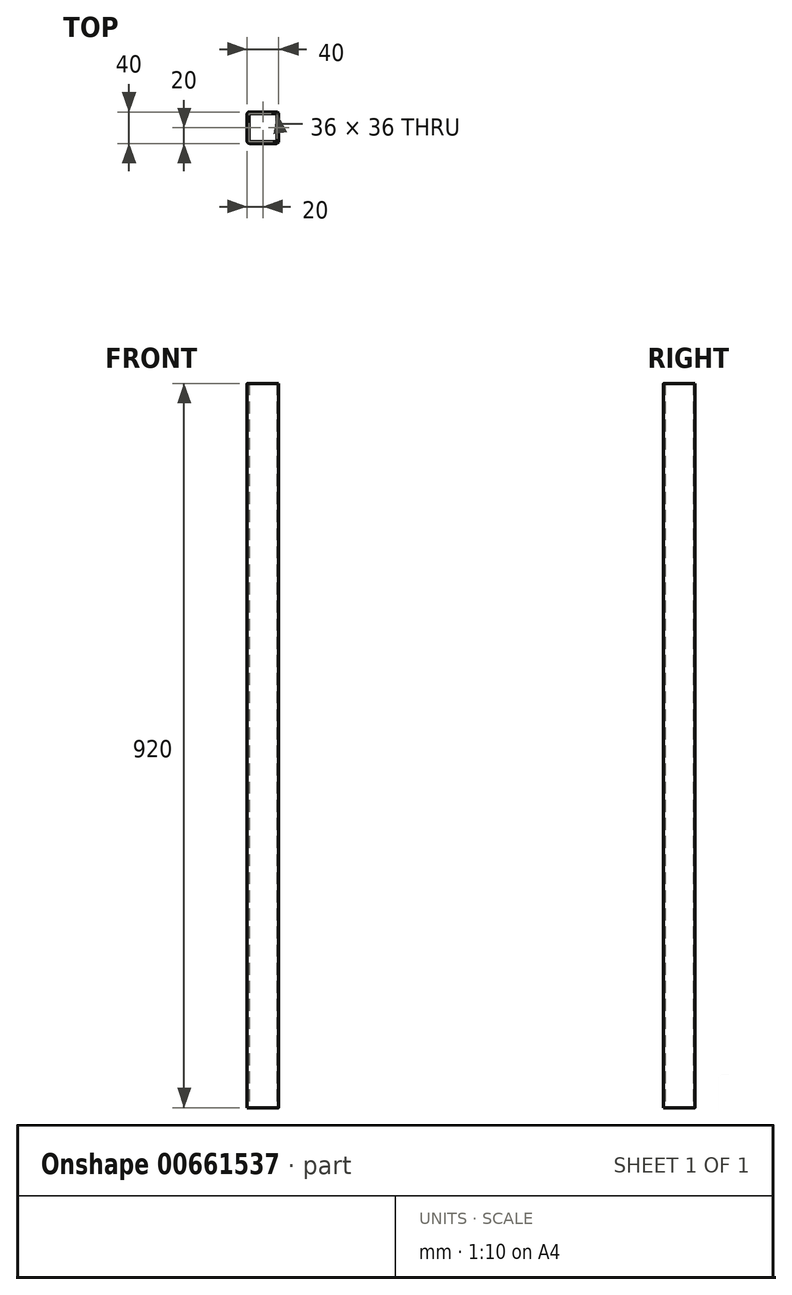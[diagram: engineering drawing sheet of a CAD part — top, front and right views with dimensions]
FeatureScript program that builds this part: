
annotation { "Feature Type Name" : "Feature", "Feature Type Description" : "" }
export const myFeature = defineFeature(function(context is Context, id is Id, definition is map)
    precondition{}
    {
        {
            var Q0;
            Q0=qCreatedBy(makeId("Top.planeOp"),FACE);
            var sketch = newSketch(context, id + "F0", { "sketchPlane" : qUnion([Q0])});
            skLineSegment(sketch, "E0.bottom", {"start": v(-17, 20) * mm, "end": v(17, 20) * mm});
            skLineSegment(sketch, "E0.top", {"start": v(-17, -20) * mm, "end": v(17, -20) * mm});
            skLineSegment(sketch, "E0.left", {"start": v(-20, 17) * mm, "end": v(-20, -17) * mm});
            skLineSegment(sketch, "E0.right", {"start": v(20, 17) * mm, "end": v(20, -17) * mm});
            skPoint(sketch, "E0.middle", {"position": v(0, 0) * mm});
            skPoint(sketch, "E1.visualSharp", {"position": v(-20, 20) * mm});
            skArc(sketch, "E1.filletArc", {"start": v(-17, 20) * mm, "mid": v(-19.12, 19.12) * mm, "end": v(-20, 17) * mm});
            skPoint(sketch, "E2.visualSharp", {"position": v(20, 20) * mm});
            skArc(sketch, "E2.filletArc", {"start": v(20, 17) * mm, "mid": v(19.12, 19.12) * mm, "end": v(17, 20) * mm});
            skPoint(sketch, "E3.visualSharp", {"position": v(20, -20) * mm});
            skArc(sketch, "E3.filletArc", {"start": v(17, -20) * mm, "mid": v(19.12, -19.12) * mm, "end": v(20, -17) * mm});
            skPoint(sketch, "E4.visualSharp", {"position": v(-20, -20) * mm});
            skArc(sketch, "E4.filletArc", {"start": v(-20, -17) * mm, "mid": v(-19.12, -19.12) * mm, "end": v(-17, -20) * mm});
            skLineSegment(sketch, "E5.0", {"start": v(-18, 18) * mm, "end": v(-18, -18) * mm});
            skLineSegment(sketch, "E5.1", {"start": v(-18, 18) * mm, "end": v(18, 18) * mm});
            skLineSegment(sketch, "E5.2", {"start": v(18, 18) * mm, "end": v(18, -18) * mm});
            skLineSegment(sketch, "E5.3", {"start": v(-18, -18) * mm, "end": v(18, -18) * mm});
            skSolve(sketch);
        }
        {
            var Q0;
            Q0=makeQuery(id+"F0.imprint","IMPRINT",FACE,{"disambiguationData":[TD([[makeQuery(id+"F0.imprint","IMPRINT",EDGE,{"derivedFrom":sQuery(id+"F0.wireOp",EDGE,"E0.bottom")}),-1.0]])]});
            extrude(context, id + "F1", {"entities" : qUnion([Q0]), "depth" : 920 * mm, "offsetDistance" : 25 * mm});
        }
    });
